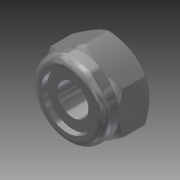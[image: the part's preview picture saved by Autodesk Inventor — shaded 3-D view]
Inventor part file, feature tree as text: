
AUTODESK INVENTOR PART (.ipt)
format: ipt  version: 2015 SP1 (Build 190203100, 203)  size: 153,600 bytes
history: native  units: in
note: dims shown in document units (in); Inventor stores cm internally (conversion verified against a paired STEP export)
features: fillet x1, other x1, imported_body x1
ambient origin geometry x8: Origin, YZ Plane, XZ Plane, XY Plane, X Axis, Y Axis, Z Axis, Center Point
bodies: Body1 (feature_tree)
feature tree (3):
  fillet  "Fillet1"  [1 undecoded]
  other  "#10 LockNut.ipt1"
  imported_body  "Base1"
note: 1 required parameter value undecoded (feature->parameter linkage not recoverable at this tier; creation-order binding heuristic only, values carry confidence <= 0.55)
